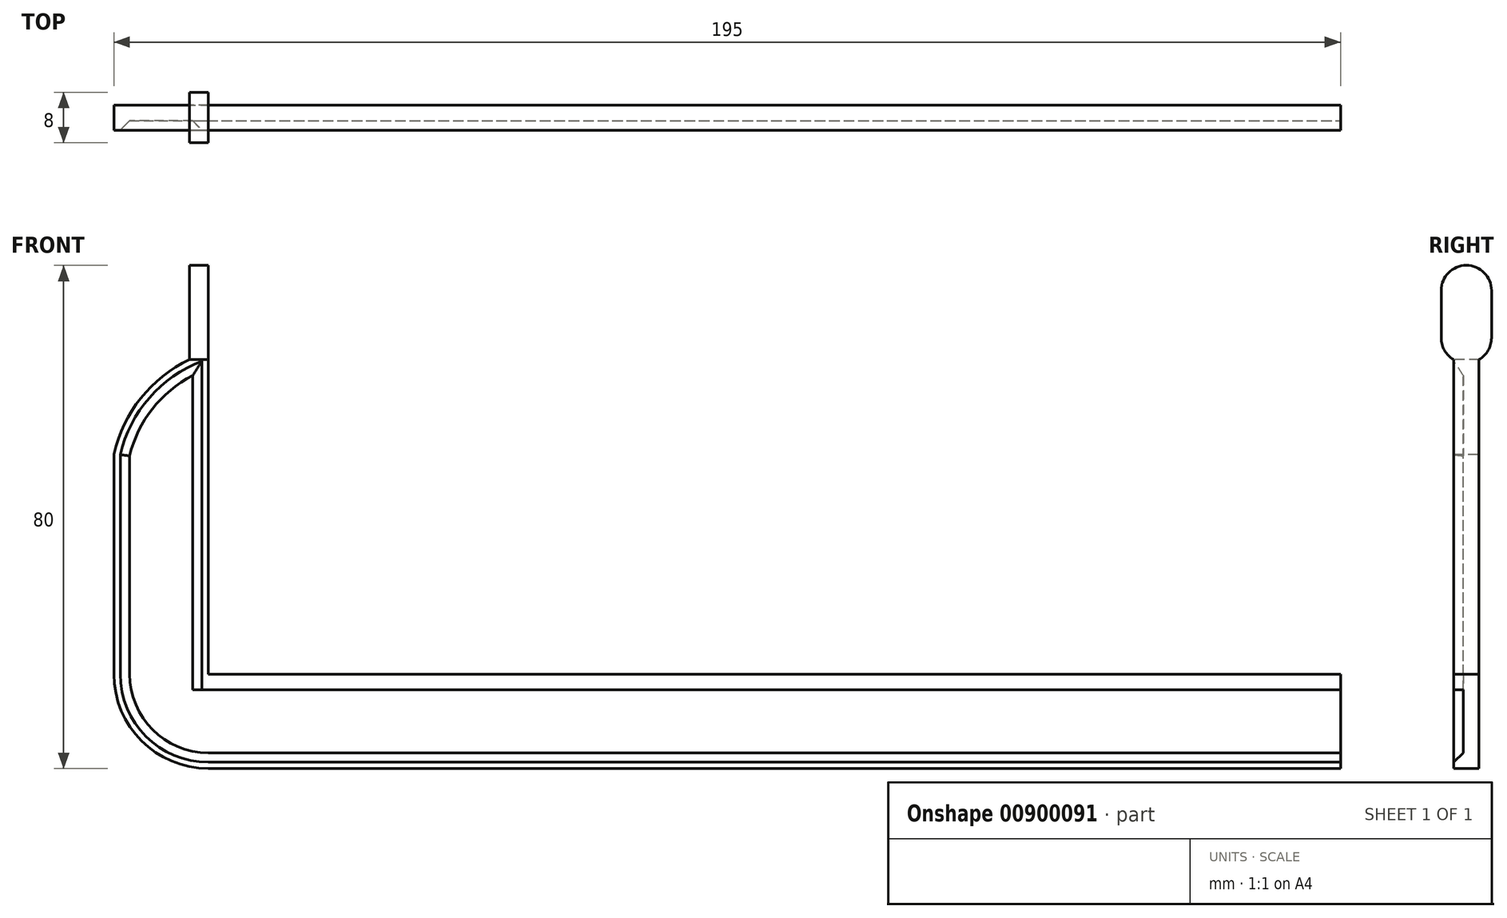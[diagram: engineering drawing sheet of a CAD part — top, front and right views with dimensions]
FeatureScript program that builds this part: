
annotation { "Feature Type Name" : "Feature", "Feature Type Description" : "" }
export const myFeature = defineFeature(function(context is Context, id is Id, definition is map)
    precondition{}
    {
        {
            var Q0;
            Q0=qCreatedBy(makeId("Front.planeOp"),FACE);
            var sketch = newSketch(context, id + "F0", { "sketchPlane" : qUnion([Q0])});
            skLineSegment(sketch, "E0.bottom", {"start": v(0, 0) * mm, "end": v(-15, 0) * mm});
            skLineSegment(sketch, "E0.top", {"start": v(0, 35) * mm, "end": v(-15, 35) * mm});
            skLineSegment(sketch, "E0.left", {"start": v(0, 0) * mm, "end": v(0, 35) * mm});
            skLineSegment(sketch, "E0.right", {"start": v(-15, 0) * mm, "end": v(-15, 35) * mm});
            skLineSegment(sketch, "E1.bottom", {"start": v(0, 0) * mm, "end": v(180, 0) * mm});
            skLineSegment(sketch, "E1.top", {"start": v(0, -15) * mm, "end": v(180, -15) * mm});
            skLineSegment(sketch, "E1.left", {"start": v(0, 0) * mm, "end": v(0, -15) * mm});
            skLineSegment(sketch, "E1.right", {"start": v(180, 0) * mm, "end": v(180, -15) * mm});
            skArc(sketch, "E2", {"start": v(-15, 0) * mm, "mid": v(-10.6, -10.6) * mm, "end": v(0, -15) * mm});
            skLineSegment(sketch, "E3", {"start": v(0, 35) * mm, "end": v(0, 55) * mm});
            skLineSegment(sketch, "E4", {"start": v(0, 55) * mm, "end": v(-4, 55) * mm});
            skLineSegment(sketch, "E5", {"start": v(-4, 55) * mm, "end": v(-4, 42) * mm});
            skSolve(sketch);
        }
        {
            var Q0;
            Q0=makeQuery(id+"F0.imprint","IMPRINT",FACE,{"disambiguationData":[TD([[makeQuery(id+"F0.imprint","IMPRINT",EDGE,{"derivedFrom":sQuery(id+"F0.wireOp",EDGE,"E0.bottom")}),-1.0]])]});
            var Q1;
            Q1=makeQuery(id+"F0.imprint","IMPRINT",FACE,{"disambiguationData":[TD([[makeQuery(id+"F0.imprint","IMPRINT",EDGE,{"derivedFrom":sQuery(id+"F0.wireOp",EDGE,"E0.bottom")}),1.0]])]});
            var Q2;
            Q2=makeQuery(id+"F0.imprint","IMPRINT",FACE,{"disambiguationData":[TD([[makeQuery(id+"F0.imprint","IMPRINT",EDGE,{"derivedFrom":sQuery(id+"F0.wireOp",EDGE,"E1.bottom")}),-1.0]])]});
            extrude(context, id + "F1", {"entities" : qUnion([Q0, Q1, Q2]), "depth" : 4 * mm, "offsetDistance" : 25 * mm});
        }
        {
            var Q0;
            Q0=makeQuery(id+"F1.opExtrude","CAP_FACE",FACE,{"disambiguationData":[OSD([sQuery(id+"F0.wireOp",EDGE,"E0.top"),sQuery(id+"F0.wireOp",EDGE,"E0.left"),sQuery(id+"F0.wireOp",EDGE,"E0.right"),sQuery(id+"F0.wireOp",EDGE,"E1.bottom"),sQuery(id+"F0.wireOp",EDGE,"E1.top"),sQuery(id+"F0.wireOp",EDGE,"E1.right"),sQuery(id+"F0.wireOp",EDGE,"E2")])],"isStart":false});
            var sketch = newSketch(context, id + "F2", { "sketchPlane" : qUnion([Q0])});
            skLineSegment(sketch, "E6", {"start": v(0, 35) * mm, "end": v(0, 65) * mm});
            skLineSegment(sketch, "E7", {"start": v(0, 65) * mm, "end": v(-3, 65) * mm});
            skLineSegment(sketch, "E8", {"start": v(-3, 65) * mm, "end": v(-3, 50) * mm});
            skArc(sketch, "E9", {"start": v(-3, 50) * mm, "mid": v(-10.72, 43.88) * mm, "end": v(-15, 35) * mm});
            skSolve(sketch);
        }
        {
            var Q0;
            Q0 = qSketchRegion(id + "F2", true);
            var Q1;
            Q1=makeQuery(id+"F2.imprint","IMPRINT",FACE,{"disambiguationData":[TD([[makeQuery(id+"F2.imprint","IMPRINT",EDGE,{"derivedFrom":sQuery(id+"F2.wireOp",EDGE,"E6")}),1.0]])]});
            extrude(context, id + "F3", {"entities" : qUnion([Q0, Q1]), "operationType" : NewBodyOperationType.ADD, "oppositeDirection" : true, "depth" : 4 * mm, "offsetDistance" : 25 * mm});
        }
        {
            var Q0;
            {var subQ0=sQuery(id+"F0.wireOp",EDGE,"E0.top");Q0=makeQuery(id+"F3.boolean.opBoolean","MERGE",FACE,{"derivedFrom":[makeQuery(id+"F1.opExtrude","CAP_FACE",FACE,{"disambiguationData":[OSD([subQ0,sQuery(id+"F0.wireOp",EDGE,"E0.left"),sQuery(id+"F0.wireOp",EDGE,"E0.right"),sQuery(id+"F0.wireOp",EDGE,"E1.bottom"),sQuery(id+"F0.wireOp",EDGE,"E1.top"),sQuery(id+"F0.wireOp",EDGE,"E1.right"),sQuery(id+"F0.wireOp",EDGE,"E2")])],"isStart":false}),makeQuery(id+"F3.opExtrude","CAP_FACE",FACE,{"disambiguationData":[OSD([subQ0,sQuery(id+"F2.wireOp",EDGE,"E6"),sQuery(id+"F2.wireOp",EDGE,"E7"),sQuery(id+"F2.wireOp",EDGE,"E8"),sQuery(id+"F2.wireOp",EDGE,"E9")])],"isStart":true})]});}
            shell(context, id + "F4", {"entities" : qUnion([Q0]), "thickness" : 2.5 * mm});
        }
        {
            var Q0;
            {var subQ0=sQuery(id+"F0.wireOp",EDGE,"E0.top");Q0=makeQuery(id+"F3.boolean.opBoolean","MERGE",FACE,{"derivedFrom":[makeQuery(id+"F1.opExtrude","CAP_FACE",FACE,{"disambiguationData":[OSD([subQ0,sQuery(id+"F0.wireOp",EDGE,"E0.left"),sQuery(id+"F0.wireOp",EDGE,"E0.right"),sQuery(id+"F0.wireOp",EDGE,"E1.bottom"),sQuery(id+"F0.wireOp",EDGE,"E1.top"),sQuery(id+"F0.wireOp",EDGE,"E1.right"),sQuery(id+"F0.wireOp",EDGE,"E2")])],"isStart":false}),makeQuery(id+"F3.opExtrude","CAP_FACE",FACE,{"disambiguationData":[OSD([subQ0,sQuery(id+"F2.wireOp",EDGE,"E6"),sQuery(id+"F2.wireOp",EDGE,"E7"),sQuery(id+"F2.wireOp",EDGE,"E8"),sQuery(id+"F2.wireOp",EDGE,"E9")])],"isStart":true})]});}
            var sketch = newSketch(context, id + "F5", { "sketchPlane" : qUnion([Q0])});
            skLineSegment(sketch, "E10", {"start": v(177.5, -2.5) * mm, "end": v(180, -2.5) * mm});
            skLineSegment(sketch, "E11", {"start": v(177.5, -12.5) * mm, "end": v(180, -12.5) * mm});
            skSolve(sketch);
        }
        {
            var Q0;
            {var subQ0=sQuery(id+"F5.wireOp",EDGE,"E10");Q0=makeQuery(id+"F5.imprint","IMPRINT",FACE,{"disambiguationData":[TD([[makeQuery(id+"F5.imprint","IMPRINT",EDGE,{"derivedFrom":subQ0}),-1.0]])]});}
            extrude(context, id + "F6", {"entities" : qUnion([Q0]), "operationType" : NewBodyOperationType.REMOVE, "oppositeDirection" : true, "depth" : 1.5 * mm, "offsetDistance" : 25 * mm});
        }
        {
            var Q0;
            {var subQ0=sQuery(id+"F0.wireOp",EDGE,"E0.top");Q0=makeQuery(id+"F3.boolean.opBoolean","MERGE",FACE,{"derivedFrom":[makeQuery(id+"F1.opExtrude","CAP_FACE",FACE,{"disambiguationData":[OSD([subQ0,sQuery(id+"F0.wireOp",EDGE,"E0.left"),sQuery(id+"F0.wireOp",EDGE,"E0.right"),sQuery(id+"F0.wireOp",EDGE,"E1.bottom"),sQuery(id+"F0.wireOp",EDGE,"E1.top"),sQuery(id+"F0.wireOp",EDGE,"E1.right"),sQuery(id+"F0.wireOp",EDGE,"E2")])],"isStart":false}),makeQuery(id+"F3.opExtrude","CAP_FACE",FACE,{"disambiguationData":[OSD([subQ0,sQuery(id+"F2.wireOp",EDGE,"E6"),sQuery(id+"F2.wireOp",EDGE,"E7"),sQuery(id+"F2.wireOp",EDGE,"E8"),sQuery(id+"F2.wireOp",EDGE,"E9")])],"isStart":true})]});}
            var sketch = newSketch(context, id + "F7", { "sketchPlane" : qUnion([Q0])});
            skLineSegment(sketch, "E12", {"start": v(0, 50) * mm, "end": v(-3, 50) * mm});
            skSolve(sketch);
        }
        {
            var Q0;
            {var subQ0=sQuery(id+"F7.wireOp",EDGE,"E12");Q0=makeQuery(id+"F7.imprint","IMPRINT",FACE,{"disambiguationData":[TD([[makeQuery(id+"F7.imprint","IMPRINT",EDGE,{"derivedFrom":subQ0}),-1.0]])]});}
            extrude(context, id + "F8", {"entities" : qUnion([Q0]), "operationType" : NewBodyOperationType.ADD, "depth" : 2 * mm, "offsetDistance" : 25 * mm});
        }
        {
            var Q0;
            {var subQ0=sQuery(id+"F0.wireOp",EDGE,"E0.top");Q0=makeQuery(id+"F3.boolean.opBoolean","MERGE",FACE,{"derivedFrom":[makeQuery(id+"F1.opExtrude","CAP_FACE",FACE,{"disambiguationData":[OSD([subQ0,sQuery(id+"F0.wireOp",EDGE,"E0.left"),sQuery(id+"F0.wireOp",EDGE,"E0.right"),sQuery(id+"F0.wireOp",EDGE,"E1.bottom"),sQuery(id+"F0.wireOp",EDGE,"E1.top"),sQuery(id+"F0.wireOp",EDGE,"E1.right"),sQuery(id+"F0.wireOp",EDGE,"E2")])],"isStart":true}),makeQuery(id+"F3.opExtrude","CAP_FACE",FACE,{"disambiguationData":[OSD([subQ0,sQuery(id+"F2.wireOp",EDGE,"E6"),sQuery(id+"F2.wireOp",EDGE,"E7"),sQuery(id+"F2.wireOp",EDGE,"E8"),sQuery(id+"F2.wireOp",EDGE,"E9")])],"isStart":false})]});}
            var sketch = newSketch(context, id + "F9", { "sketchPlane" : qUnion([Q0])});
            skLineSegment(sketch, "E13", {"start": v(0, 50) * mm, "end": v(3, 50) * mm});
            skSolve(sketch);
        }
        {
            var Q0;
            {var subQ0=sQuery(id+"F9.wireOp",EDGE,"E13");Q0=makeQuery(id+"F9.imprint","IMPRINT",FACE,{"disambiguationData":[TD([[makeQuery(id+"F9.imprint","IMPRINT",EDGE,{"derivedFrom":subQ0}),1.0]])]});}
            extrude(context, id + "F10", {"entities" : qUnion([Q0]), "operationType" : NewBodyOperationType.ADD, "depth" : 2 * mm, "offsetDistance" : 25 * mm});
        }
        {
            var Q0;
            Q0=makeQuery(id+"F8.opExtrude","CAP_EDGE",EDGE,{"disambiguationData":[OSD([sQuery(id+"F7.wireOp",EDGE,"E12")])],"isStart":false});
            var Q1;
            Q1=makeQuery(id+"F10.opExtrude","CAP_EDGE",EDGE,{"disambiguationData":[OSD([sQuery(id+"F9.wireOp",EDGE,"E13")])],"isStart":false});
            var Q2;
            Q2=makeQuery(id+"F10.opExtrude","CAP_EDGE",EDGE,{"disambiguationData":[OSD([sQuery(id+"F2.wireOp",EDGE,"E7")])],"isStart":false});
            var Q3;
            Q3=makeQuery(id+"F8.opExtrude","CAP_EDGE",EDGE,{"disambiguationData":[OSD([sQuery(id+"F2.wireOp",EDGE,"E7")])],"isStart":false});
            fillet(context, id + "F11", {"entities" : qUnion([Q0, Q1, Q2, Q3]), "radius" : 4 * mm, "tangentPropagation" : true, "allowEdgeOverflow" : false});
        }
        {
            var Q0;
            {var subQ0=sQuery(id+"F2.wireOp",EDGE,"E9");Q0=makeQuery(id+"F4.opShell","OFFSET_EDGE",EDGE,{"disambiguationData":[OSD([subQ0]),TDD([makeQuery(id+"F3.opExtrude","CAP_EDGE",EDGE,{"disambiguationData":[OSD([subQ0])],"isStart":true})])]});}
            var Q1;
            {var subQ0=sQuery(id+"F2.wireOp",EDGE,"E6");var subQ1=sQuery(id+"F0.wireOp",EDGE,"E0.left");Q1=makeQuery(id+"F4.opShell","OFFSET_EDGE",EDGE,{"disambiguationData":[OSD([subQ1,subQ0]),TDD([makeQuery(id+"F3.boolean.opBoolean","MERGE",EDGE,{"derivedFrom":[makeQuery(id+"F1.opExtrude","CAP_EDGE",EDGE,{"disambiguationData":[OSD([subQ1])],"isStart":false}),makeQuery(id+"F3.opExtrude","CAP_EDGE",EDGE,{"disambiguationData":[OSD([subQ0])],"isStart":true})]})])]});}
            var Q2;
            {var subQ0=sQuery(id+"F0.wireOp",EDGE,"E0.right");Q2=makeQuery(id+"F4.opShell","OFFSET_EDGE",EDGE,{"disambiguationData":[OSD([subQ0]),TDD([makeQuery(id+"F1.opExtrude","CAP_EDGE",EDGE,{"disambiguationData":[OSD([subQ0])],"isStart":false})])]});}
            var Q3;
            {var subQ0=sQuery(id+"F0.wireOp",EDGE,"E1.top");Q3=makeQuery(id+"F6.boolean.opBoolean","MERGE",EDGE,{"derivedFrom":[makeQuery(id+"F4.opShell","OFFSET_EDGE",EDGE,{"disambiguationData":[OSD([subQ0]),TDD([makeQuery(id+"F1.opExtrude","CAP_EDGE",EDGE,{"disambiguationData":[OSD([subQ0])],"isStart":false})])]})],"fromTools":[makeQuery(id+"F6.opExtrude","CAP_EDGE",EDGE,{"disambiguationData":[OSD([sQuery(id+"F5.wireOp",EDGE,"E11")])],"isStart":true})]});}
            var Q4;
            {var subQ0=sQuery(id+"F0.wireOp",EDGE,"E2");Q4=makeQuery(id+"F4.opShell","OFFSET_EDGE",EDGE,{"disambiguationData":[OSD([subQ0]),TDD([makeQuery(id+"F1.opExtrude","CAP_EDGE",EDGE,{"disambiguationData":[OSD([subQ0])],"isStart":false})])]});}
            var Q5;
            {var subQ0=sQuery(id+"F0.wireOp",EDGE,"E1.bottom");Q5=makeQuery(id+"F6.boolean.opBoolean","MERGE",EDGE,{"derivedFrom":[makeQuery(id+"F4.opShell","OFFSET_EDGE",EDGE,{"disambiguationData":[OSD([subQ0]),TDD([makeQuery(id+"F1.opExtrude","CAP_EDGE",EDGE,{"disambiguationData":[OSD([subQ0])],"isStart":false})])]})],"fromTools":[makeQuery(id+"F6.opExtrude","CAP_EDGE",EDGE,{"disambiguationData":[OSD([sQuery(id+"F5.wireOp",EDGE,"E10")])],"isStart":true})]});}
            chamfer(context, id + "F12", {"entities" : qUnion([Q0, Q1, Q2, Q3, Q4, Q5]), "width" : 1.5 * mm, "tangentPropagation" : true});
        }
    });
